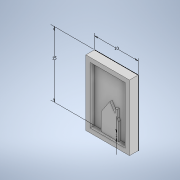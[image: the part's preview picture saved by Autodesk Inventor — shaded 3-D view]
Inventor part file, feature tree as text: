
AUTODESK INVENTOR PART (.ipt)
format: ipt  version: 2022 (Build 260153000, 153)  size: 133,120 bytes
history: native  units: mm
features: sketch x3, extrude x3
ambient origin geometry x8: Origin, YZ Plane, XZ Plane, XY Plane, X Axis, Y Axis, Z Axis, Center Point
bodies: Solid1 (feature_tree)
feature tree (6):
  sketch  "Sketch1"  dims[d0=10.0mm d1=15.0mm]
  extrude  "Extrusion1"  Depth=15.0mm
  sketch  "Sketch2"  dims[d2=1.0mm d3=1.0mm d4=0.0mm]
  extrude  "Extrusion2"  Depth=1.0mm TaperAngle=0.0deg
  extrude  "Extrusion3"  Depth=4.0mm
  sketch  "Sketch3"  dims[d5=2.0mm d6=0.0mm d7=4.0mm d8=4.0mm d9=2.0mm d10=3.0mm d11=1.0mm d12=0.5mm d13=0.5mm d14=0.0mm]
